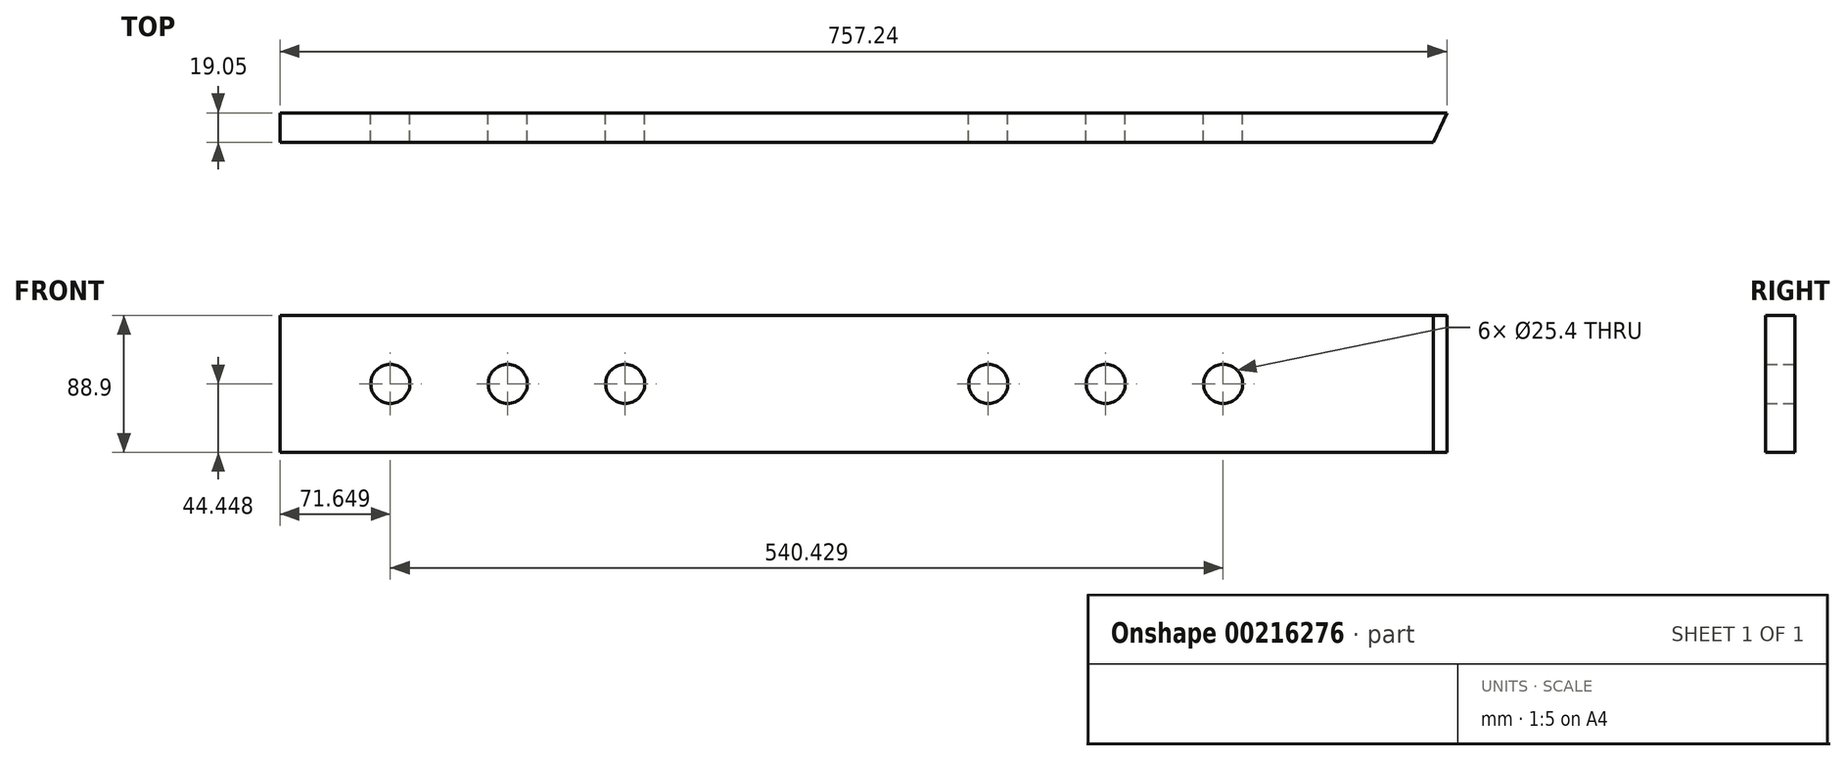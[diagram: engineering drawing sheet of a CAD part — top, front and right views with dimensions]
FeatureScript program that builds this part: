
annotation { "Feature Type Name" : "Feature", "Feature Type Description" : "" }
export const myFeature = defineFeature(function(context is Context, id is Id, definition is map)
    precondition{}
    {
        {
            var Q0;
            Q0=qCreatedBy(makeId("Front.planeOp"),FACE);
            var sketch = newSketch(context, id + "F0", { "sketchPlane" : qUnion([Q0])});
            skLineSegment(sketch, "E0", {"start": v(-4407.94, -2196.25) * mm, "end": v(-3650.7, -2196.25) * mm});
            skLineSegment(sketch, "E1", {"start": v(-3650.7, -2196.25) * mm, "end": v(-3650.7, -2285.15) * mm});
            skLineSegment(sketch, "E2", {"start": v(-3650.7, -2285.15) * mm, "end": v(-4407.94, -2285.15) * mm});
            skLineSegment(sketch, "E3", {"start": v(-4407.94, -2285.15) * mm, "end": v(-4407.94, -2196.25) * mm});
            skCircle(sketch, "E4", {"center": v(-4336.3, -2240.7) * mm, "radius": 12.7 * mm});
            skCircle(sketch, "E5", {"center": v(-4260.1, -2240.7) * mm, "radius": 12.7 * mm});
            skCircle(sketch, "E6", {"center": v(-4183.9, -2240.7) * mm, "radius": 12.7 * mm});
            skCircle(sketch, "E7", {"center": v(-3948.26, -2240.7) * mm, "radius": 12.7 * mm});
            skCircle(sketch, "E8", {"center": v(-3872.06, -2240.7) * mm, "radius": 12.7 * mm});
            skCircle(sketch, "E9", {"center": v(-3795.86, -2240.7) * mm, "radius": 12.7 * mm});
            skLineSegment(sketch, "E10", {"start": v(-4407.94, -2240.7) * mm, "end": v(-3650.93, -2240.7) * mm, "construction": true});
            skSolve(sketch);
        }
        {
            var Q0;
            Q0=makeQuery(id+"F0.imprint","IMPRINT",FACE,{"disambiguationData":[TD([[makeQuery(id+"F0.imprint","IMPRINT",EDGE,{"derivedFrom":sQuery(id+"F0.wireOp",EDGE,"E0")}),-1.0]])]});
            extrude(context, id + "F1", {"entities" : qUnion([Q0]), "depth" : 19.05 * mm});
        }
        {
            var Q0;
            Q0=makeQuery(id+"F1.opExtrude","SWEPT_FACE",FACE,{"disambiguationData":[OSD([sQuery(id+"F0.wireOp",EDGE,"E2")])]});
            var sketch = newSketch(context, id + "F2", { "sketchPlane" : qUnion([Q0])});
            skLineSegment(sketch, "E11", {"start": v(-3650.7, 0) * mm, "end": v(-3650.7, 19.05) * mm});
            skLineSegment(sketch, "E12", {"start": v(-3650.7, 19.05) * mm, "end": v(-3659.55, 19.05) * mm});
            skLineSegment(sketch, "E13", {"start": v(-3659.55, 19.05) * mm, "end": v(-3650.7, 0) * mm});
            skSolve(sketch);
        }
        {
            var Q0;
            Q0=makeQuery(id+"F2.imprint","IMPRINT",FACE,{"disambiguationData":[TD([[makeQuery(id+"F2.imprint","IMPRINT",EDGE,{"derivedFrom":sQuery(id+"F2.wireOp",EDGE,"E11")}),-1.0]])]});
            extrude(context, id + "F3", {"entities" : qUnion([Q0]), "operationType" : NewBodyOperationType.REMOVE, "endBound" : BoundingType.THROUGH_ALL, "oppositeDirection" : true, "depth" : 25.4 * mm});
        }
    });
